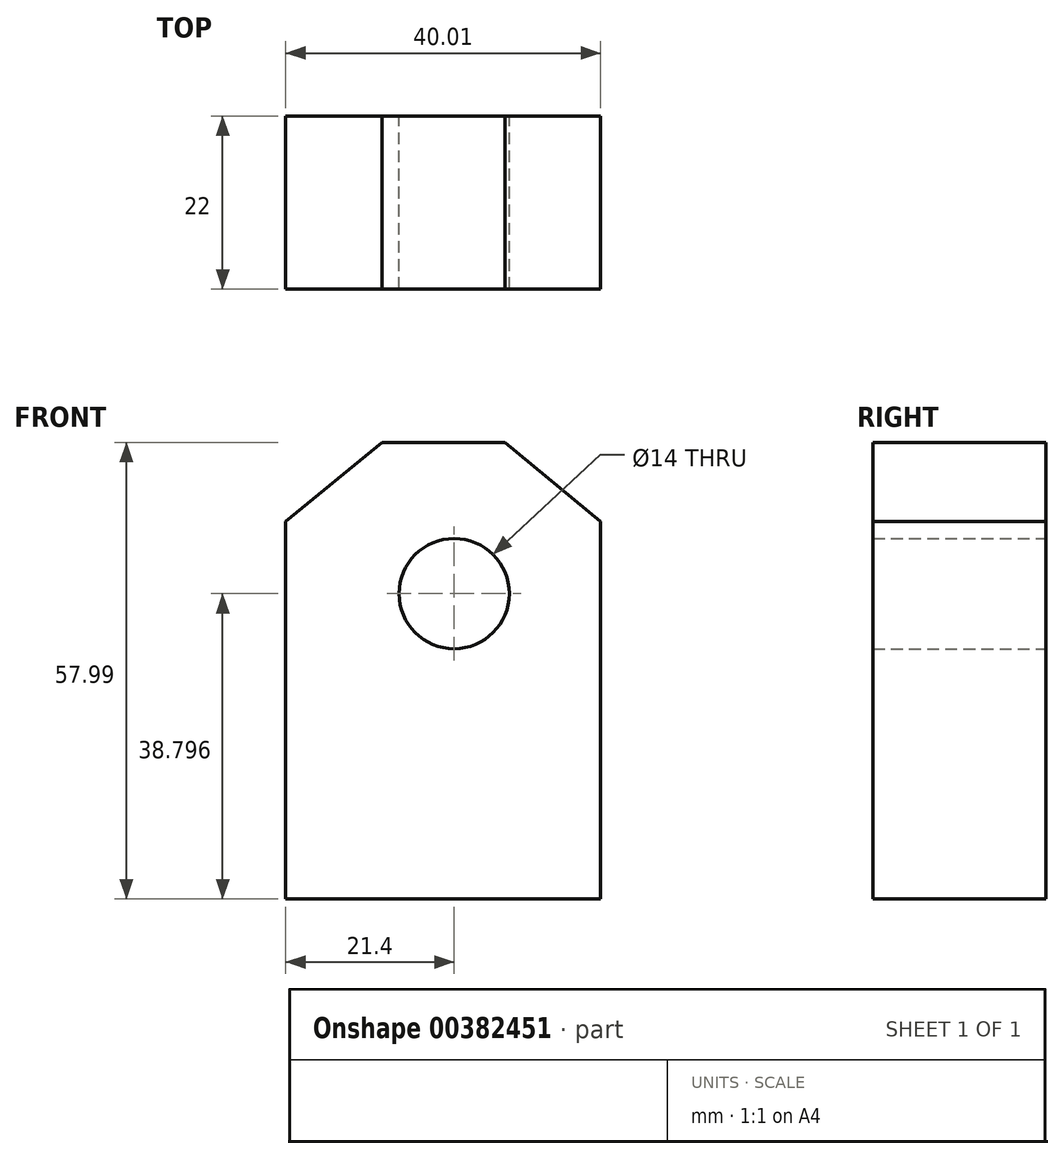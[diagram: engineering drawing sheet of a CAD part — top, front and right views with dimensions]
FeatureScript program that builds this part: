
annotation { "Feature Type Name" : "Feature", "Feature Type Description" : "" }
export const myFeature = defineFeature(function(context is Context, id is Id, definition is map)
    precondition{}
    {
        {
            var Q0;
            Q0=qCreatedBy(makeId("Front.planeOp"),FACE);
            var sketch = newSketch(context, id + "F0", { "sketchPlane" : qUnion([Q0])});
            skLineSegment(sketch, "E0", {"start": v(18.6, 0) * mm, "end": v(-21.4, 0) * mm});
            skLineSegment(sketch, "E1", {"start": v(-21.4, 0) * mm, "end": v(-21.4, 47.98) * mm});
            skLineSegment(sketch, "E2", {"start": v(18.6, 0) * mm, "end": v(18.6, 47.98) * mm});
            skLineSegment(sketch, "E3", {"start": v(-21.4, 47.98) * mm, "end": v(-9.15, 57.99) * mm});
            skLineSegment(sketch, "E4", {"start": v(-9.15, 57.99) * mm, "end": v(6.47, 57.99) * mm});
            skLineSegment(sketch, "E5", {"start": v(6.47, 57.99) * mm, "end": v(18.6, 47.98) * mm});
            skCircle(sketch, "E6", {"center": v(0, 38.8) * mm, "radius": 7 * mm});
            skSolve(sketch);
        }
        {
            var Q0;
            Q0=makeQuery(id+"F0.imprint","IMPRINT",FACE,{"disambiguationData":[TD([[makeQuery(id+"F0.imprint","IMPRINT",EDGE,{"derivedFrom":sQuery(id+"F0.wireOp",EDGE,"E0")}),-1.0]])]});
            extrude(context, id + "F1", {"entities" : qUnion([Q0]), "depth" : 22 * mm});
        }
    });
